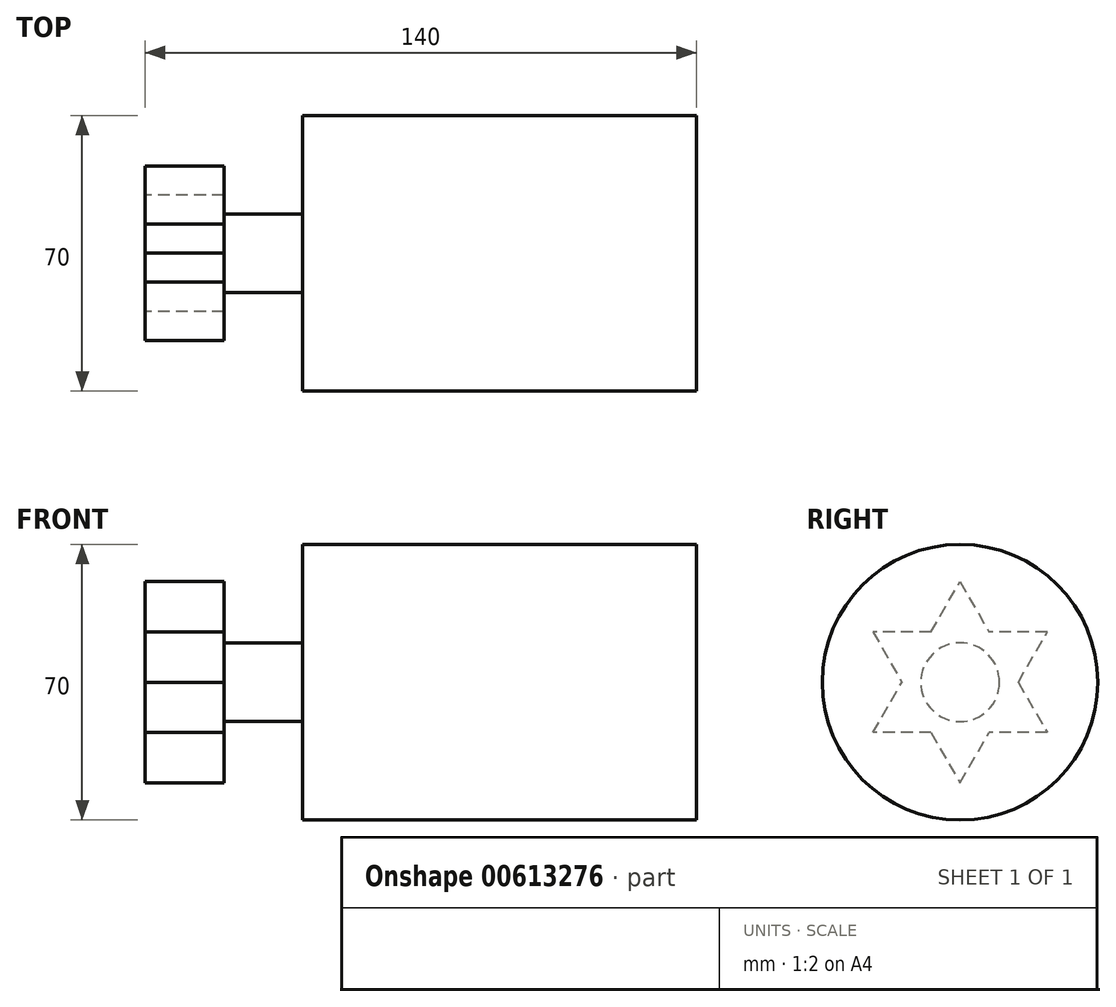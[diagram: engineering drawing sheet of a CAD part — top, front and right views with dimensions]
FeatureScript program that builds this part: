
annotation { "Feature Type Name" : "Feature", "Feature Type Description" : "" }
export const myFeature = defineFeature(function(context is Context, id is Id, definition is map)
    precondition{}
    {
        {
            var Q0;
            Q0=qCreatedBy(makeId("Right.planeOp"),FACE);
            var sketch = newSketch(context, id + "F0", { "sketchPlane" : qUnion([Q0])});
            skCircle(sketch, "E0", {"center": v(0, 0) * mm, "radius": 35 * mm});
            skSolve(sketch);
        }
        {
            var Q0;
            Q0 = qSketchRegion(id + "F0", true);
            extrude(context, id + "F1", {"entities" : qUnion([Q0]), "depth" : 100 * mm, "offsetDistance" : 25 * mm});
        }
        {
            var Q0;
            Q0=makeQuery(id+"F1.opExtrude","CAP_FACE",FACE,{"disambiguationData":[OSD([sQuery(id+"F0.wireOp",EDGE,"E0")])],"isStart":true});
            var sketch = newSketch(context, id + "F2", { "sketchPlane" : qUnion([Q0])});
            skCircle(sketch, "E1", {"center": v(0, 0) * mm, "radius": 10 * mm});
            skSolve(sketch);
        }
        {
            var Q0;
            Q0 = qSketchRegion(id + "F2", true);
            extrude(context, id + "F3", {"entities" : qUnion([Q0]), "operationType" : NewBodyOperationType.ADD, "depth" : 40 * mm, "offsetDistance" : 25 * mm});
        }
        {
            var Q0;
            Q0=makeQuery(id+"F3.opExtrude","CAP_FACE",FACE,{"disambiguationData":[OSD([sQuery(id+"F2.wireOp",EDGE,"E1")])],"isStart":false});
            var sketch = newSketch(context, id + "F4", { "sketchPlane" : qUnion([Q0])});
            skCircle(sketch, "E2.cCircle", {"center": v(0, 0) * mm, "radius": 25.56 * mm, "construction": true});
            skLineSegment(sketch, "E2.0", {"start": v(0, -25.56) * mm, "end": v(-22.13, 12.78) * mm});
            skLineSegment(sketch, "E2.1", {"start": v(-22.13, 12.78) * mm, "end": v(22.13, 12.78) * mm});
            skLineSegment(sketch, "E2.2", {"start": v(22.13, 12.78) * mm, "end": v(0, -25.56) * mm});
            skLineSegment(sketch, "E3.0", {"start": v(0, 25.56) * mm, "end": v(22.13, -12.78) * mm, "construction": true});
            skLineSegment(sketch, "E3.1", {"start": v(22.13, -12.78) * mm, "end": v(-22.13, -12.78) * mm, "construction": true});
            skLineSegment(sketch, "E3.2", {"start": v(-22.13, -12.78) * mm, "end": v(0, 25.56) * mm, "construction": true});
            skLineSegment(sketch, "E4", {"start": v(-22.13, -12.78) * mm, "end": v(22.13, -12.78) * mm});
            skLineSegment(sketch, "E5", {"start": v(22.13, -12.78) * mm, "end": v(0, 25.56) * mm});
            skLineSegment(sketch, "E6", {"start": v(0, 25.56) * mm, "end": v(-22.13, -12.78) * mm});
            skSolve(sketch);
        }
        {
            var Q0;
            Q0 = qSketchRegion(id + "F4", true);
            extrude(context, id + "F5", {"entities" : qUnion([Q0]), "operationType" : NewBodyOperationType.ADD, "oppositeDirection" : true, "depth" : 20 * mm, "offsetDistance" : 25 * mm});
        }
    });
